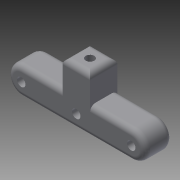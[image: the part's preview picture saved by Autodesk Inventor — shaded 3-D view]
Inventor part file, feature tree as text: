
AUTODESK INVENTOR PART (.ipt)
format: ipt  version: 2015 (Build 190159000, 159)  size: 150,528 bytes
history: native  units: mm
features: sketch x5, hole x3, extrude x2, fillet x1
ambient origin geometry x8: Origin, YZ Plane, XZ Plane, XY Plane, X Axis, Y Axis, Z Axis, Center Point
bodies: Solid1 (feature_tree)
feature tree (11):
  extrude  "Extrusion1"  Depth=10.0mm TaperAngle=0.0deg
  hole  "Hole1"  [1 undecoded]
  hole  "Hole2"  [1 undecoded]
  extrude  "Extrusion2"  [1 undecoded]
  fillet  "Fillet1"  [1 undecoded]
  hole  "Hole3"  [1 undecoded]
  sketch  "Sketch1"  dims[d2=40.0mm d3=10.0mm d4=0.0mm]
  sketch  "Sketch2"  dims[d5=3.1mm d6=6.0mm d7=4.0mm d8=5.0mm d9=90.0deg d10=8.0mm d11=20.594885mm]
  sketch  "Sketch3"  dims[d12=3.1mm d13=6.0mm d14=4.0mm d15=5.0mm d16=90.0deg d17=8.0mm d18=20.594885mm d19=10.0mm]
  sketch  "Sketch4"  dims[d20=5.0mm d21=10.0mm d22=0.0mm]
  sketch  "Sketch5"  dims[d23=2.0mm d24=3.1mm d25=6.0mm d26=4.0mm d27=5.0mm d28=90.0deg d29=8.0mm d30=0.0mm]
note: 5 required parameter values undecoded (feature->parameter linkage not recoverable at this tier; creation-order binding heuristic only, values carry confidence <= 0.55)
